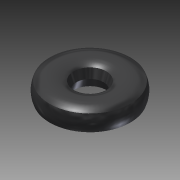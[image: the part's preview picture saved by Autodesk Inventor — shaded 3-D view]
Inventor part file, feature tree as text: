
AUTODESK INVENTOR PART (.ipt)
format: ipt  version: 2013 (Build 170138000, 138)  size: 135,680 bytes
history: native  units: in
note: dims shown in document units (in); Inventor stores cm internally (conversion verified against a paired STEP export)
features: revolve x1, sketch x1
ambient origin geometry x8: Origin, YZ Plane, XZ Plane, XY Plane, X Axis, Y Axis, Z Axis, Center Point
bodies: Solid1 (feature_tree)
feature tree (2):
  revolve  "Revolution1"  [1 undecoded]
  sketch  "Sketch1"  dims[d1=0.375in d2=0.3125in d4=0.1875in d5=0.5in d6=90.0deg d7=0.9688in d8=0.1875in d9=0.93in]
note: 1 required parameter value undecoded (feature->parameter linkage not recoverable at this tier; creation-order binding heuristic only, values carry confidence <= 0.55)
